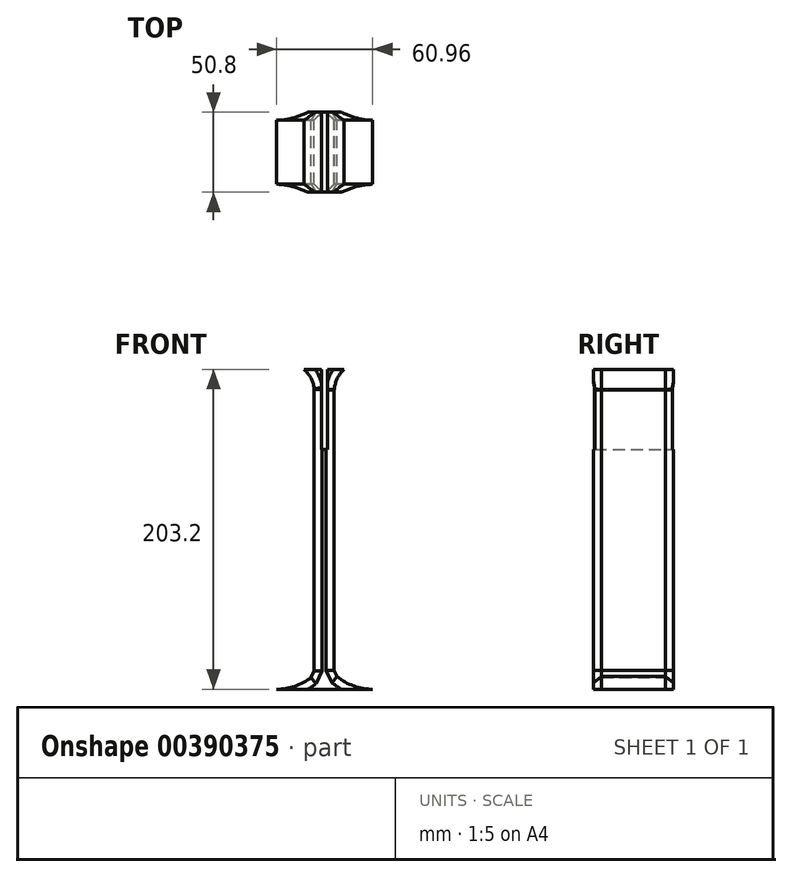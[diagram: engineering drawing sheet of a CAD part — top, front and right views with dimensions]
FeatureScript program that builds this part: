
annotation { "Feature Type Name" : "Feature", "Feature Type Description" : "" }
export const myFeature = defineFeature(function(context is Context, id is Id, definition is map)
    precondition{}
    {
        {
            var Q0;
            Q0=qCreatedBy(makeId("Front.planeOp"),FACE);
            var sketch = newSketch(context, id + "F0", { "sketchPlane" : qUnion([Q0])});
            skLineSegment(sketch, "E0", {"start": v(0, 160.47) * mm, "end": v(0, -42.73) * mm});
            skLineSegment(sketch, "E1", {"start": v(0, -42.73) * mm, "end": v(30.48, -42.73) * mm});
            skLineSegment(sketch, "E2", {"start": v(0, -42.73) * mm, "end": v(-30.48, -42.73) * mm});
            skLineSegment(sketch, "E3", {"start": v(0, 160.47) * mm, "end": v(12.18, 160.47) * mm});
            skLineSegment(sketch, "E4", {"start": v(0, 160.47) * mm, "end": v(-13.22, 160.47) * mm});
            skArc(sketch, "E5", {"start": v(-30.48, -42.73) * mm, "mid": v(-12.97, -38.12) * mm, "end": v(0, -25.48) * mm});
            skArc(sketch, "E6", {"start": v(0, -25.48) * mm, "mid": v(12.97, -38.12) * mm, "end": v(30.48, -42.73) * mm});
            skLineSegment(sketch, "E7", {"start": v(-6.61, 160.47) * mm, "end": v(-6.61, -42.73) * mm});
            skLineSegment(sketch, "E8", {"start": v(6.09, 160.47) * mm, "end": v(6.09, -42.73) * mm});
            skArc(sketch, "E9", {"start": v(-6.61, 144.51) * mm, "mid": v(-7.92, 153.32) * mm, "end": v(-13.22, 160.47) * mm});
            skArc(sketch, "E10", {"start": v(12.18, 160.47) * mm, "mid": v(7.35, 153.17) * mm, "end": v(6.09, 144.51) * mm});
            skSolve(sketch);
        }
        {
            var Q0;
            Q0 = qSketchRegion(id + "F0", true);
            extrude(context, id + "F1", {"entities" : qUnion([Q0]), "depth" : 50.8 * mm});
        }
        {
            var Q0;
            Q0=makeQuery(id+"F1.opExtrude","CAP_EDGE",EDGE,{"disambiguationData":[OSD([sQuery(id+"F0.wireOp",EDGE,"E8")])],"isStart":true});
            var Q1;
            Q1=makeQuery(id+"F1.opExtrude","SWEPT_FACE",FACE,{"disambiguationData":[OSD([sQuery(id+"F0.wireOp",EDGE,"E7")])]});
            var Q2;
            Q2=makeQuery(id+"F1.opExtrude","SWEPT_FACE",FACE,{"disambiguationData":[OSD([sQuery(id+"F0.wireOp",EDGE,"E8")])]});
            chamfer(context, id + "F2", {"entities" : qUnion([Q0, Q1, Q2]), "width" : 5.08 * mm, "tangentPropagation" : true});
        }
        {
            var Q0;
            Q0=makeQuery(id+"F1.opExtrude","SWEPT_FACE",FACE,{"disambiguationData":[OSD([sQuery(id+"F0.wireOp",EDGE,"E3"),sQuery(id+"F0.wireOp",EDGE,"E4")])]});
            var sketch = newSketch(context, id + "F3", { "sketchPlane" : qUnion([Q0])});
            skLineSegment(sketch, "E11", {"start": v(0, -48.75) * mm, "end": v(0, 0) * mm});
            skPoint(sketch, "E11.startSnap0", {"position": v(-0.3, -48.75) * mm});
            skLineSegment(sketch, "E12", {"start": v(0, 0) * mm, "end": v(-2.14, 0) * mm});
            skLineSegment(sketch, "E13", {"start": v(0, 0) * mm, "end": v(1.86, 0) * mm});
            skLineSegment(sketch, "E14", {"start": v(1.86, 0) * mm, "end": v(1.86, -50.8) * mm});
            skLineSegment(sketch, "E15", {"start": v(1.86, -50.8) * mm, "end": v(-2.14, -50.8) * mm});
            skLineSegment(sketch, "E16", {"start": v(-2.14, -50.8) * mm, "end": v(-2.14, 0) * mm});
            skSolve(sketch);
        }
        {
            var Q0;
            Q0 = qSketchRegion(id + "F3", true);
            extrude(context, id + "F4", {"entities" : qUnion([Q0]), "operationType" : NewBodyOperationType.REMOVE, "oppositeDirection" : true, "depth" : 50.8 * mm});
        }
    });
